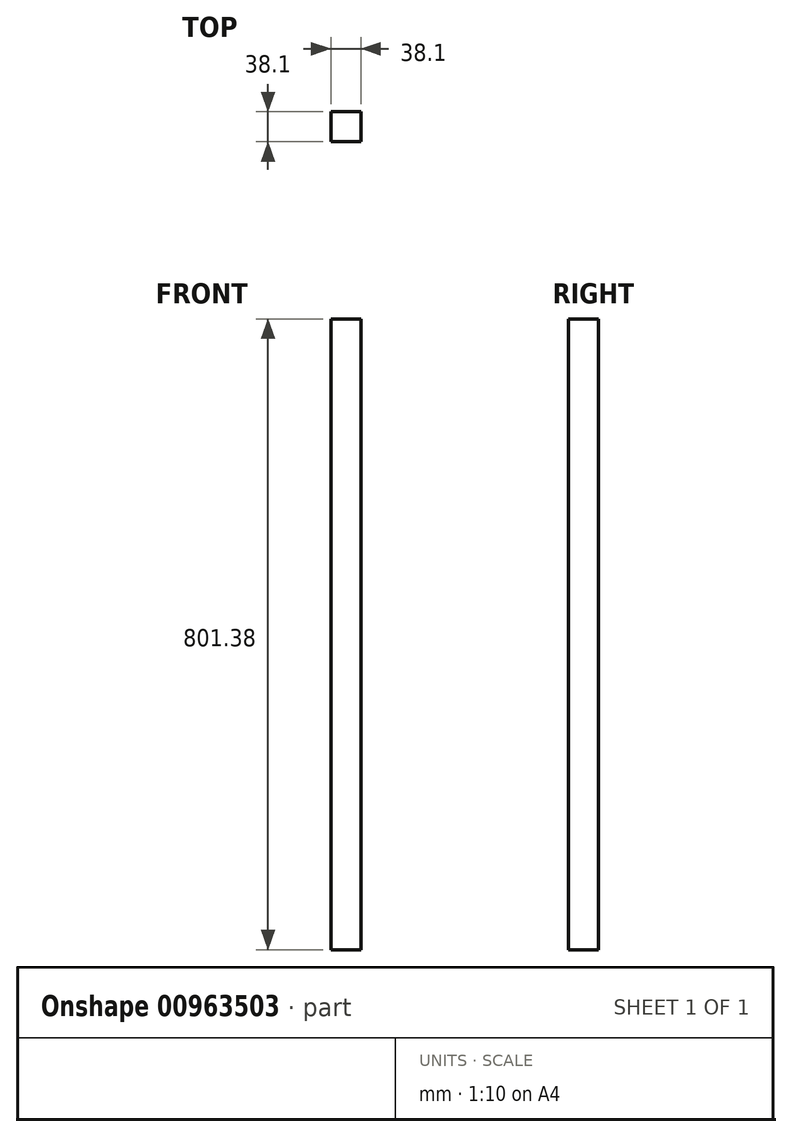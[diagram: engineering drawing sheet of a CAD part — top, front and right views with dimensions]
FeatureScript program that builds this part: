
annotation { "Feature Type Name" : "Feature", "Feature Type Description" : "" }
export const myFeature = defineFeature(function(context is Context, id is Id, definition is map)
    precondition{}
    {
        {
            var Q0;
            Q0=qCreatedBy(makeId("Front.planeOp"),FACE);
            var sketch = newSketch(context, id + "F0", { "sketchPlane" : qUnion([Q0])});
            skLineSegment(sketch, "E0.bottom", {"start": v(-19.05, -400.69) * mm, "end": v(19.05, -400.69) * mm});
            skLineSegment(sketch, "E0.top", {"start": v(-19.05, 400.69) * mm, "end": v(19.05, 400.69) * mm});
            skLineSegment(sketch, "E0.left", {"start": v(-19.05, -400.69) * mm, "end": v(-19.05, 400.69) * mm});
            skLineSegment(sketch, "E0.right", {"start": v(19.05, -400.69) * mm, "end": v(19.05, 400.69) * mm});
            skPoint(sketch, "E0.middle", {"position": v(0, 0) * mm});
            skSolve(sketch);
        }
        {
            var Q0;
            Q0=qSketchRegion(id+"F0",true);
            extrude(context, id + "F1", {"entities" : qUnion([Q0]), "depth" : 38.1 * mm, "offsetDistance" : 25.4 * mm});
        }
    });
